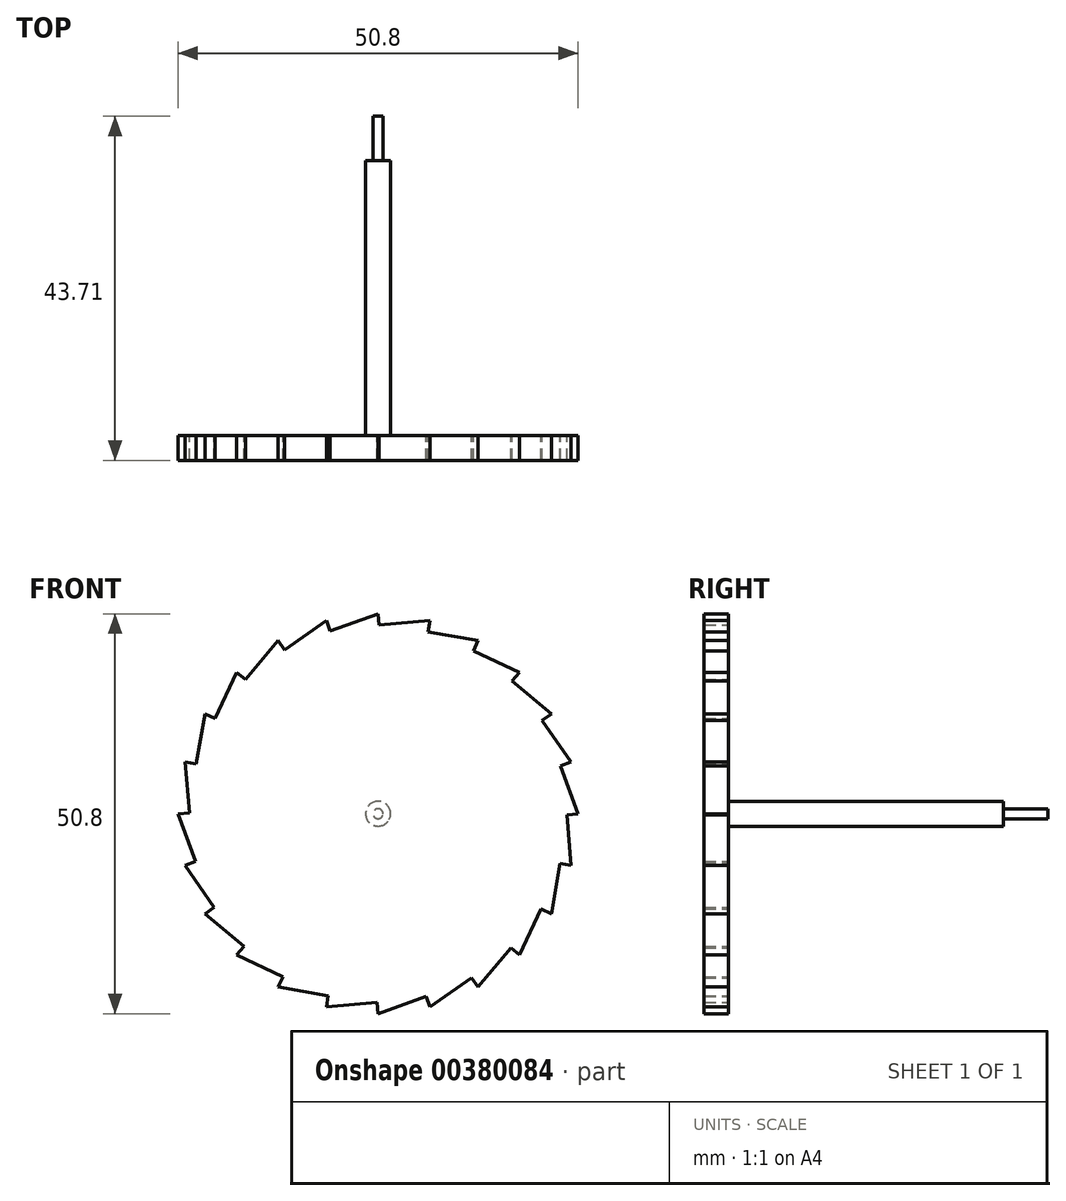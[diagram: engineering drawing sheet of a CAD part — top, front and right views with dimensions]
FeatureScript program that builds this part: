
annotation { "Feature Type Name" : "Feature", "Feature Type Description" : "" }
export const myFeature = defineFeature(function(context is Context, id is Id, definition is map)
    precondition{}
    {
        {
            var Q0;
            Q0=qCreatedBy(makeId("Front.planeOp"),FACE);
            var sketch = newSketch(context, id + "F0", { "sketchPlane" : qUnion([Q0])});
            skLineSegment(sketch, "E0", {"start": v(0, 0) * mm, "end": v(0, 25.4) * mm, "construction": true});
            skLineSegment(sketch, "E1", {"start": v(-7.2, 25.4) * mm, "end": v(0, 25.4) * mm, "construction": true});
            skLineSegment(sketch, "E2", {"start": v(0, 0) * mm, "end": v(-6.57, 24.53) * mm, "construction": true});
            skLineSegment(sketch, "E3.anchor2", {"start": v(0, 0) * mm, "end": v(0, 12.68) * mm, "construction": true});
            skLineSegment(sketch, "E4", {"start": v(0, 25.4) * mm, "end": v(-6.08, 23.19) * mm});
            skLineSegment(sketch, "E5", {"start": v(-6.08, 23.19) * mm, "end": v(-6.57, 24.53) * mm});
            skLineSegment(sketch, "E6.1.0", {"start": v(6.57, 24.53) * mm, "end": v(0.13, 23.97) * mm});
            skLineSegment(sketch, "E6.1.1", {"start": v(0.13, 23.97) * mm, "end": v(0, 25.4) * mm});
            skLineSegment(sketch, "E6.2.0", {"start": v(12.7, 22) * mm, "end": v(6.32, 23.12) * mm});
            skLineSegment(sketch, "E6.2.1", {"start": v(6.32, 23.12) * mm, "end": v(6.57, 24.53) * mm});
            skLineSegment(sketch, "E6.3.0", {"start": v(17.96, 17.96) * mm, "end": v(12.1, 20.7) * mm});
            skLineSegment(sketch, "E6.3.1", {"start": v(12.1, 20.7) * mm, "end": v(12.7, 22) * mm});
            skLineSegment(sketch, "E6.4.0", {"start": v(22, 12.7) * mm, "end": v(17.04, 16.86) * mm});
            skLineSegment(sketch, "E6.4.1", {"start": v(17.04, 16.86) * mm, "end": v(17.96, 17.96) * mm});
            skLineSegment(sketch, "E6.5.0", {"start": v(24.53, 6.57) * mm, "end": v(20.82, 11.88) * mm});
            skLineSegment(sketch, "E6.5.1", {"start": v(20.82, 11.88) * mm, "end": v(22, 12.7) * mm});
            skLineSegment(sketch, "E6.6.0", {"start": v(25.4, 0) * mm, "end": v(23.19, 6.08) * mm});
            skLineSegment(sketch, "E6.6.1", {"start": v(23.19, 6.08) * mm, "end": v(24.53, 6.57) * mm});
            skLineSegment(sketch, "E6.7.0", {"start": v(24.53, -6.57) * mm, "end": v(23.97, -0.13) * mm});
            skLineSegment(sketch, "E6.7.1", {"start": v(23.97, -0.13) * mm, "end": v(25.4, 0) * mm});
            skLineSegment(sketch, "E6.8.0", {"start": v(22, -12.7) * mm, "end": v(23.12, -6.32) * mm});
            skLineSegment(sketch, "E6.8.1", {"start": v(23.12, -6.32) * mm, "end": v(24.53, -6.57) * mm});
            skLineSegment(sketch, "E6.9.0", {"start": v(17.96, -17.96) * mm, "end": v(20.7, -12.1) * mm});
            skLineSegment(sketch, "E6.9.1", {"start": v(20.7, -12.1) * mm, "end": v(22, -12.7) * mm});
            skLineSegment(sketch, "E6.10.0", {"start": v(12.7, -22) * mm, "end": v(16.86, -17.04) * mm});
            skLineSegment(sketch, "E6.10.1", {"start": v(16.86, -17.04) * mm, "end": v(17.96, -17.96) * mm});
            skLineSegment(sketch, "E6.11.0", {"start": v(6.57, -24.53) * mm, "end": v(11.88, -20.82) * mm});
            skLineSegment(sketch, "E6.11.1", {"start": v(11.88, -20.82) * mm, "end": v(12.7, -22) * mm});
            skLineSegment(sketch, "E6.12.0", {"start": v(0, -25.4) * mm, "end": v(6.08, -23.19) * mm});
            skLineSegment(sketch, "E6.12.1", {"start": v(6.08, -23.19) * mm, "end": v(6.57, -24.53) * mm});
            skLineSegment(sketch, "E6.13.0", {"start": v(-6.57, -24.53) * mm, "end": v(-0.13, -23.97) * mm});
            skLineSegment(sketch, "E6.13.1", {"start": v(-0.13, -23.97) * mm, "end": v(0, -25.4) * mm});
            skLineSegment(sketch, "E6.14.0", {"start": v(-12.7, -22) * mm, "end": v(-6.32, -23.12) * mm});
            skLineSegment(sketch, "E6.14.1", {"start": v(-6.32, -23.12) * mm, "end": v(-6.57, -24.53) * mm});
            skLineSegment(sketch, "E6.15.0", {"start": v(-17.96, -17.96) * mm, "end": v(-12.1, -20.7) * mm});
            skLineSegment(sketch, "E6.15.1", {"start": v(-12.1, -20.7) * mm, "end": v(-12.7, -22) * mm});
            skLineSegment(sketch, "E6.16.0", {"start": v(-22, -12.7) * mm, "end": v(-17.04, -16.86) * mm});
            skLineSegment(sketch, "E6.16.1", {"start": v(-17.04, -16.86) * mm, "end": v(-17.96, -17.96) * mm});
            skLineSegment(sketch, "E6.17.0", {"start": v(-24.53, -6.57) * mm, "end": v(-20.82, -11.88) * mm});
            skLineSegment(sketch, "E6.17.1", {"start": v(-20.82, -11.88) * mm, "end": v(-22, -12.7) * mm});
            skLineSegment(sketch, "E6.18.0", {"start": v(-25.4, 0) * mm, "end": v(-23.19, -6.08) * mm});
            skLineSegment(sketch, "E6.18.1", {"start": v(-23.19, -6.08) * mm, "end": v(-24.53, -6.57) * mm});
            skLineSegment(sketch, "E6.19.0", {"start": v(-24.53, 6.57) * mm, "end": v(-23.97, 0.13) * mm});
            skLineSegment(sketch, "E6.19.1", {"start": v(-23.97, 0.13) * mm, "end": v(-25.4, 0) * mm});
            skLineSegment(sketch, "E6.20.0", {"start": v(-22, 12.7) * mm, "end": v(-23.12, 6.32) * mm});
            skLineSegment(sketch, "E6.20.1", {"start": v(-23.12, 6.32) * mm, "end": v(-24.53, 6.57) * mm});
            skLineSegment(sketch, "E6.21.0", {"start": v(-17.96, 17.96) * mm, "end": v(-20.7, 12.1) * mm});
            skLineSegment(sketch, "E6.21.1", {"start": v(-20.7, 12.1) * mm, "end": v(-22, 12.7) * mm});
            skLineSegment(sketch, "E6.22.0", {"start": v(-12.7, 22) * mm, "end": v(-16.86, 17.04) * mm});
            skLineSegment(sketch, "E6.22.1", {"start": v(-16.86, 17.04) * mm, "end": v(-17.96, 17.96) * mm});
            skLineSegment(sketch, "E6.23.0", {"start": v(-6.57, 24.53) * mm, "end": v(-11.88, 20.82) * mm});
            skLineSegment(sketch, "E6.23.1", {"start": v(-11.88, 20.82) * mm, "end": v(-12.7, 22) * mm});
            skPoint(sketch, "E6.center", {"position": v(0, 0) * mm});
            skSolve(sketch);
        }
        {
            var Q0;
            Q0 = qSketchRegion(id + "F0", true);
            extrude(context, id + "F1", {"entities" : qUnion([Q0]), "offsetDistance" : 25.4 * mm, "depth" : 3.12 * mm});
        }
        {
            var Q0;
            Q0=makeQuery(id+"F1.opExtrude","CAP_FACE",FACE,{"disambiguationData":[OSD([sQuery(id+"F0.wireOp",EDGE,"E6.1.0"),sQuery(id+"F0.wireOp",EDGE,"E6.1.1"),sQuery(id+"F0.wireOp",EDGE,"E6.2.0"),sQuery(id+"F0.wireOp",EDGE,"E6.2.1"),sQuery(id+"F0.wireOp",EDGE,"E6.3.0"),sQuery(id+"F0.wireOp",EDGE,"E6.3.1"),sQuery(id+"F0.wireOp",EDGE,"E6.4.0"),sQuery(id+"F0.wireOp",EDGE,"E6.4.1"),sQuery(id+"F0.wireOp",EDGE,"E6.5.0"),sQuery(id+"F0.wireOp",EDGE,"E6.5.1"),sQuery(id+"F0.wireOp",EDGE,"E6.6.0"),sQuery(id+"F0.wireOp",EDGE,"E6.6.1"),sQuery(id+"F0.wireOp",EDGE,"E6.7.0"),sQuery(id+"F0.wireOp",EDGE,"E6.7.1"),sQuery(id+"F0.wireOp",EDGE,"E6.8.0"),sQuery(id+"F0.wireOp",EDGE,"E6.8.1"),sQuery(id+"F0.wireOp",EDGE,"E6.9.0"),sQuery(id+"F0.wireOp",EDGE,"E6.9.1"),sQuery(id+"F0.wireOp",EDGE,"E6.10.0"),sQuery(id+"F0.wireOp",EDGE,"E6.10.1"),sQuery(id+"F0.wireOp",EDGE,"E6.11.0"),sQuery(id+"F0.wireOp",EDGE,"E6.11.1"),sQuery(id+"F0.wireOp",EDGE,"E6.12.0"),sQuery(id+"F0.wireOp",EDGE,"E6.12.1"),sQuery(id+"F0.wireOp",EDGE,"E6.13.0"),sQuery(id+"F0.wireOp",EDGE,"E6.13.1"),sQuery(id+"F0.wireOp",EDGE,"E6.14.0"),sQuery(id+"F0.wireOp",EDGE,"E6.14.1"),sQuery(id+"F0.wireOp",EDGE,"E6.15.0"),sQuery(id+"F0.wireOp",EDGE,"E6.15.1"),sQuery(id+"F0.wireOp",EDGE,"E6.16.0"),sQuery(id+"F0.wireOp",EDGE,"E6.16.1"),sQuery(id+"F0.wireOp",EDGE,"E6.17.0"),sQuery(id+"F0.wireOp",EDGE,"E6.17.1"),sQuery(id+"F0.wireOp",EDGE,"E6.18.0"),sQuery(id+"F0.wireOp",EDGE,"E6.18.1"),sQuery(id+"F0.wireOp",EDGE,"E6.19.0"),sQuery(id+"F0.wireOp",EDGE,"E6.19.1"),sQuery(id+"F0.wireOp",EDGE,"E6.20.0"),sQuery(id+"F0.wireOp",EDGE,"E6.20.1"),sQuery(id+"F0.wireOp",EDGE,"E6.21.0"),sQuery(id+"F0.wireOp",EDGE,"E6.21.1"),sQuery(id+"F0.wireOp",EDGE,"E6.22.0"),sQuery(id+"F0.wireOp",EDGE,"E6.22.1"),sQuery(id+"F0.wireOp",EDGE,"E6.23.0"),sQuery(id+"F0.wireOp",EDGE,"E6.23.1"),sQuery(id+"F0.wireOp",EDGE,"E4"),sQuery(id+"F0.wireOp",EDGE,"E5")])],"isStart":true});
            var sketch = newSketch(context, id + "F2", { "sketchPlane" : qUnion([Q0])});
            skCircle(sketch, "E7", {"center": v(0, 0) * mm, "radius": 1.59 * mm});
            skSolve(sketch);
        }
        {
            var Q0;
            Q0 = qSketchRegion(id + "F2", true);
            extrude(context, id + "F3", {"entities" : qUnion([Q0]), "operationType" : NewBodyOperationType.ADD, "depth" : 34.92 * mm});
        }
        {
            var Q0;
            Q0=makeQuery(id+"F3.opExtrude","CAP_FACE",FACE,{"disambiguationData":[OSD([sQuery(id+"F2.wireOp",EDGE,"E7")])],"isStart":false});
            var sketch = newSketch(context, id + "F4", { "sketchPlane" : qUnion([Q0])});
            skCircle(sketch, "E8", {"center": v(0, 0) * mm, "radius": 0.64 * mm});
            skSolve(sketch);
        }
        {
            var Q0;
            Q0 = qSketchRegion(id + "F4", true);
            extrude(context, id + "F5", {"entities" : qUnion([Q0]), "operationType" : NewBodyOperationType.ADD, "depth" : 5.66 * mm});
        }
    });
